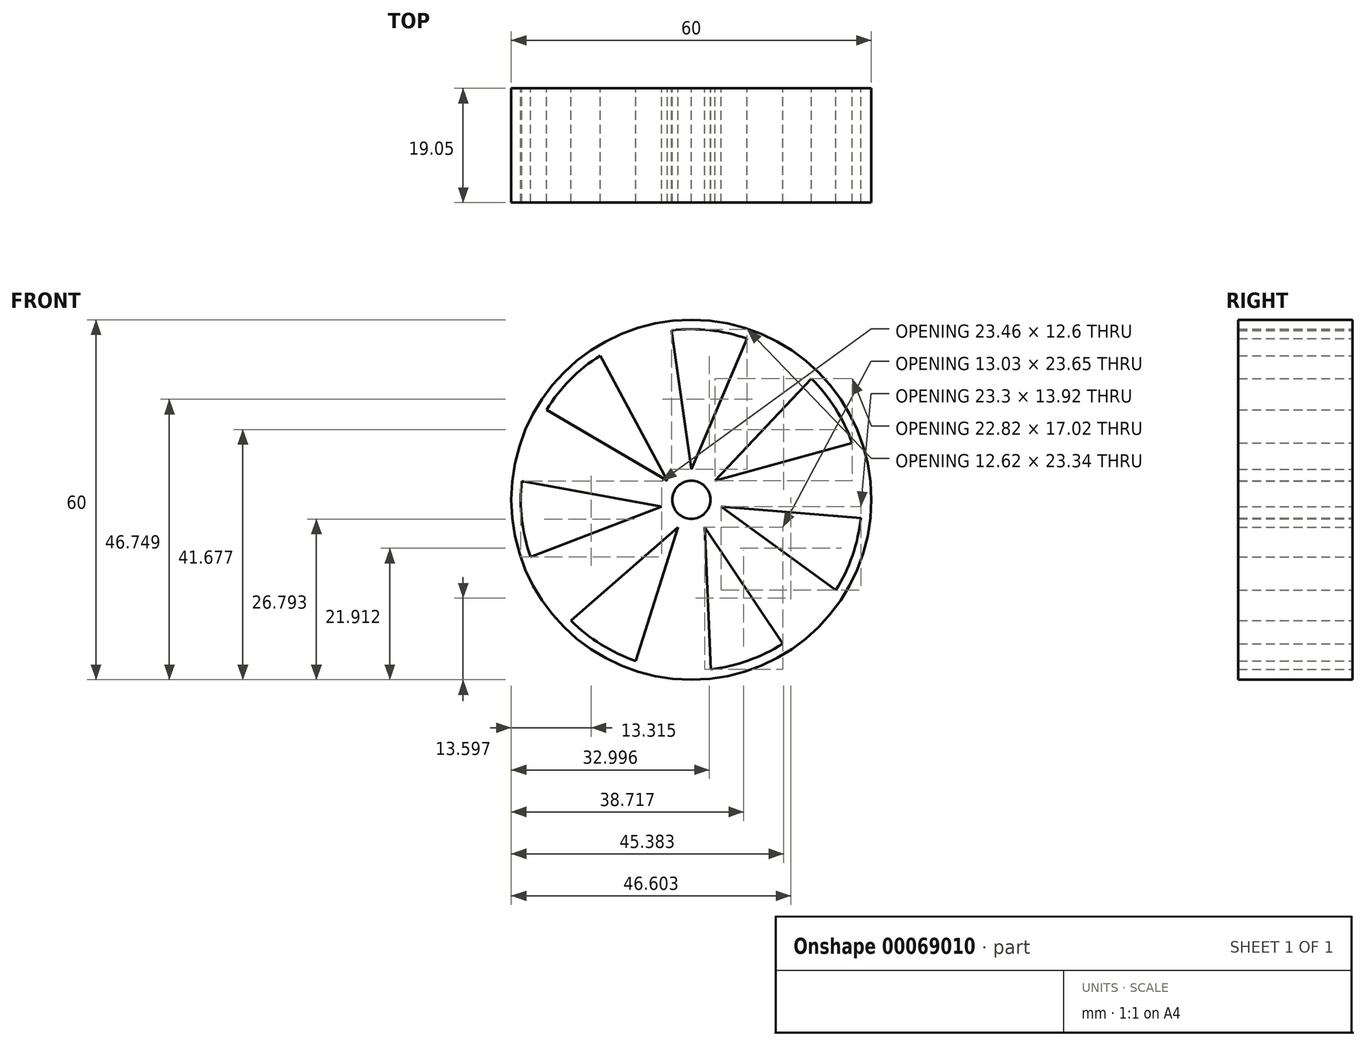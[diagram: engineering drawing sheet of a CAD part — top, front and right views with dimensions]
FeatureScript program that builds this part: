
annotation { "Feature Type Name" : "Feature", "Feature Type Description" : "" }
export const myFeature = defineFeature(function(context is Context, id is Id, definition is map)
    precondition{}
    {
        {
            var Q0;
            Q0=qCreatedBy(makeId("Front.planeOp"),FACE);
            var sketch = newSketch(context, id + "F0", { "sketchPlane" : qUnion([Q0])});
            skCircle(sketch, "E0", {"center": v(0, 0) * mm, "radius": 30 * mm});
            skCircle(sketch, "E1", {"center": v(0, 0) * mm, "radius": 3.18 * mm});
            skCircle(sketch, "E2", {"center": v(0, 0) * mm, "radius": 5.08 * mm, "construction": true});
            skCircle(sketch, "E3", {"center": v(0, 0) * mm, "radius": 28.58 * mm, "construction": true});
            skLineSegment(sketch, "E4", {"start": v(-3.33, 28.38) * mm, "end": v(0, 5.08) * mm});
            skLineSegment(sketch, "E5", {"start": v(0, 5.08) * mm, "end": v(9.37, 27) * mm});
            skLineSegment(sketch, "E6.1.0", {"start": v(-3.97, 3.17) * mm, "end": v(-15.27, 24.15) * mm});
            skLineSegment(sketch, "E6.1.1", {"start": v(-24.27, 15.09) * mm, "end": v(-3.97, 3.17) * mm});
            skLineSegment(sketch, "E6.2.0", {"start": v(-4.95, -1.13) * mm, "end": v(-28.4, 3.12) * mm});
            skLineSegment(sketch, "E6.2.1", {"start": v(-26.93, -9.57) * mm, "end": v(-4.95, -1.13) * mm});
            skLineSegment(sketch, "E6.3.0", {"start": v(-2.2, -4.58) * mm, "end": v(-20.15, -20.26) * mm});
            skLineSegment(sketch, "E6.3.1", {"start": v(-9.3, -27.02) * mm, "end": v(-2.2, -4.58) * mm});
            skLineSegment(sketch, "E6.4.0", {"start": v(2.2, -4.58) * mm, "end": v(3.28, -28.39) * mm});
            skLineSegment(sketch, "E6.4.1", {"start": v(15.32, -24.12) * mm, "end": v(2.2, -4.58) * mm});
            skLineSegment(sketch, "E6.5.0", {"start": v(4.95, -1.13) * mm, "end": v(24.24, -15.14) * mm});
            skLineSegment(sketch, "E6.5.1", {"start": v(28.41, -3.06) * mm, "end": v(4.95, -1.13) * mm});
            skLineSegment(sketch, "E6.6.0", {"start": v(3.97, 3.17) * mm, "end": v(26.95, 9.5) * mm});
            skLineSegment(sketch, "E6.6.1", {"start": v(20.1, 20.3) * mm, "end": v(3.97, 3.17) * mm});
            skCircle(sketch, "E7", {"center": v(0, 0) * mm, "radius": 5.14 * mm});
            skCircle(sketch, "E8", {"center": v(0, 0) * mm, "radius": 28.42 * mm});
            skSolve(sketch);
        }
        {
            var Q0;
            Q0=makeQuery(id+"F0.imprint","IMPRINT",FACE,{"disambiguationData":[TD([[makeQuery(id+"F0.imprint","IMPRINT",EDGE,{"derivedFrom":sQuery(id+"F0.wireOp",EDGE,"E0")}),1.0]])]});
            extrude(context, id + "F1", {"entities" : qUnion([Q0]), "depth" : 19.05 * mm});
        }
        {
            var Q0;
            {var subQ0=sQuery(id+"F0.wireOp",EDGE,"E8");var subQ1=sQuery(id+"F0.wireOp",EDGE,"E4");var subQ2=makeQuery(id+"F0.imprint","INTERSECT",VERTEX,{"derivedFrom":[subQ1,subQ0]});Q0=makeQuery(id+"F0.imprint","IMPRINT",FACE,{"disambiguationData":[TD([[makeQuery(id+"F0.imprint","IMPRINT",EDGE,{"disambiguationData":[TD([[subQ2,-1.0]])],"derivedFrom":subQ1}),-1.0]])]});}
            var Q1;
            {var subQ0=sQuery(id+"F0.wireOp",EDGE,"E8");var subQ1=sQuery(id+"F0.wireOp",EDGE,"E5");var subQ2=makeQuery(id+"F0.imprint","INTERSECT",VERTEX,{"derivedFrom":[subQ1,subQ0]});Q1=makeQuery(id+"F0.imprint","IMPRINT",FACE,{"disambiguationData":[TD([[makeQuery(id+"F0.imprint","IMPRINT",EDGE,{"disambiguationData":[TD([[subQ2,1.0]])],"derivedFrom":subQ1}),-1.0]])]});}
            var Q2;
            {var subQ0=sQuery(id+"F0.wireOp",EDGE,"E8");var subQ1=sQuery(id+"F0.wireOp",EDGE,"E6.5.1");var subQ2=makeQuery(id+"F0.imprint","INTERSECT",VERTEX,{"derivedFrom":[subQ1,subQ0]});Q2=makeQuery(id+"F0.imprint","IMPRINT",FACE,{"disambiguationData":[TD([[makeQuery(id+"F0.imprint","IMPRINT",EDGE,{"disambiguationData":[TD([[subQ2,-1.0]])],"derivedFrom":subQ1}),-1.0]])]});}
            var Q3;
            {var subQ0=sQuery(id+"F0.wireOp",EDGE,"E8");var subQ1=sQuery(id+"F0.wireOp",EDGE,"E6.4.1");var subQ2=makeQuery(id+"F0.imprint","INTERSECT",VERTEX,{"derivedFrom":[subQ1,subQ0]});Q3=makeQuery(id+"F0.imprint","IMPRINT",FACE,{"disambiguationData":[TD([[makeQuery(id+"F0.imprint","IMPRINT",EDGE,{"disambiguationData":[TD([[subQ2,-1.0]])],"derivedFrom":subQ1}),-1.0]])]});}
            var Q4;
            {var subQ0=sQuery(id+"F0.wireOp",EDGE,"E8");var subQ1=sQuery(id+"F0.wireOp",EDGE,"E6.3.1");var subQ2=makeQuery(id+"F0.imprint","INTERSECT",VERTEX,{"derivedFrom":[subQ1,subQ0]});Q4=makeQuery(id+"F0.imprint","IMPRINT",FACE,{"disambiguationData":[TD([[makeQuery(id+"F0.imprint","IMPRINT",EDGE,{"disambiguationData":[TD([[subQ2,-1.0]])],"derivedFrom":subQ1}),-1.0]])]});}
            var Q5;
            {var subQ0=sQuery(id+"F0.wireOp",EDGE,"E8");var subQ1=sQuery(id+"F0.wireOp",EDGE,"E6.2.1");var subQ2=makeQuery(id+"F0.imprint","INTERSECT",VERTEX,{"derivedFrom":[subQ1,subQ0]});Q5=makeQuery(id+"F0.imprint","IMPRINT",FACE,{"disambiguationData":[TD([[makeQuery(id+"F0.imprint","IMPRINT",EDGE,{"disambiguationData":[TD([[subQ2,-1.0]])],"derivedFrom":subQ1}),-1.0]])]});}
            var Q6;
            {var subQ0=sQuery(id+"F0.wireOp",EDGE,"E8");var subQ1=sQuery(id+"F0.wireOp",EDGE,"E6.1.1");var subQ2=makeQuery(id+"F0.imprint","INTERSECT",VERTEX,{"derivedFrom":[subQ1,subQ0]});Q6=makeQuery(id+"F0.imprint","IMPRINT",FACE,{"disambiguationData":[TD([[makeQuery(id+"F0.imprint","IMPRINT",EDGE,{"disambiguationData":[TD([[subQ2,-1.0]])],"derivedFrom":subQ1}),-1.0]])]});}
            var Q7;
            Q7=makeQuery(id+"F0.imprint","IMPRINT",FACE,{"disambiguationData":[TD([[makeQuery(id+"F0.imprint","IMPRINT",EDGE,{"derivedFrom":sQuery(id+"F0.wireOp",EDGE,"E1")}),-1.0]])]});
            extrude(context, id + "F2", {"entities" : qUnion([Q0, Q1, Q2, Q3, Q4, Q5, Q6, Q7]), "operationType" : NewBodyOperationType.ADD, "depth" : 19.05 * mm});
        }
    });
